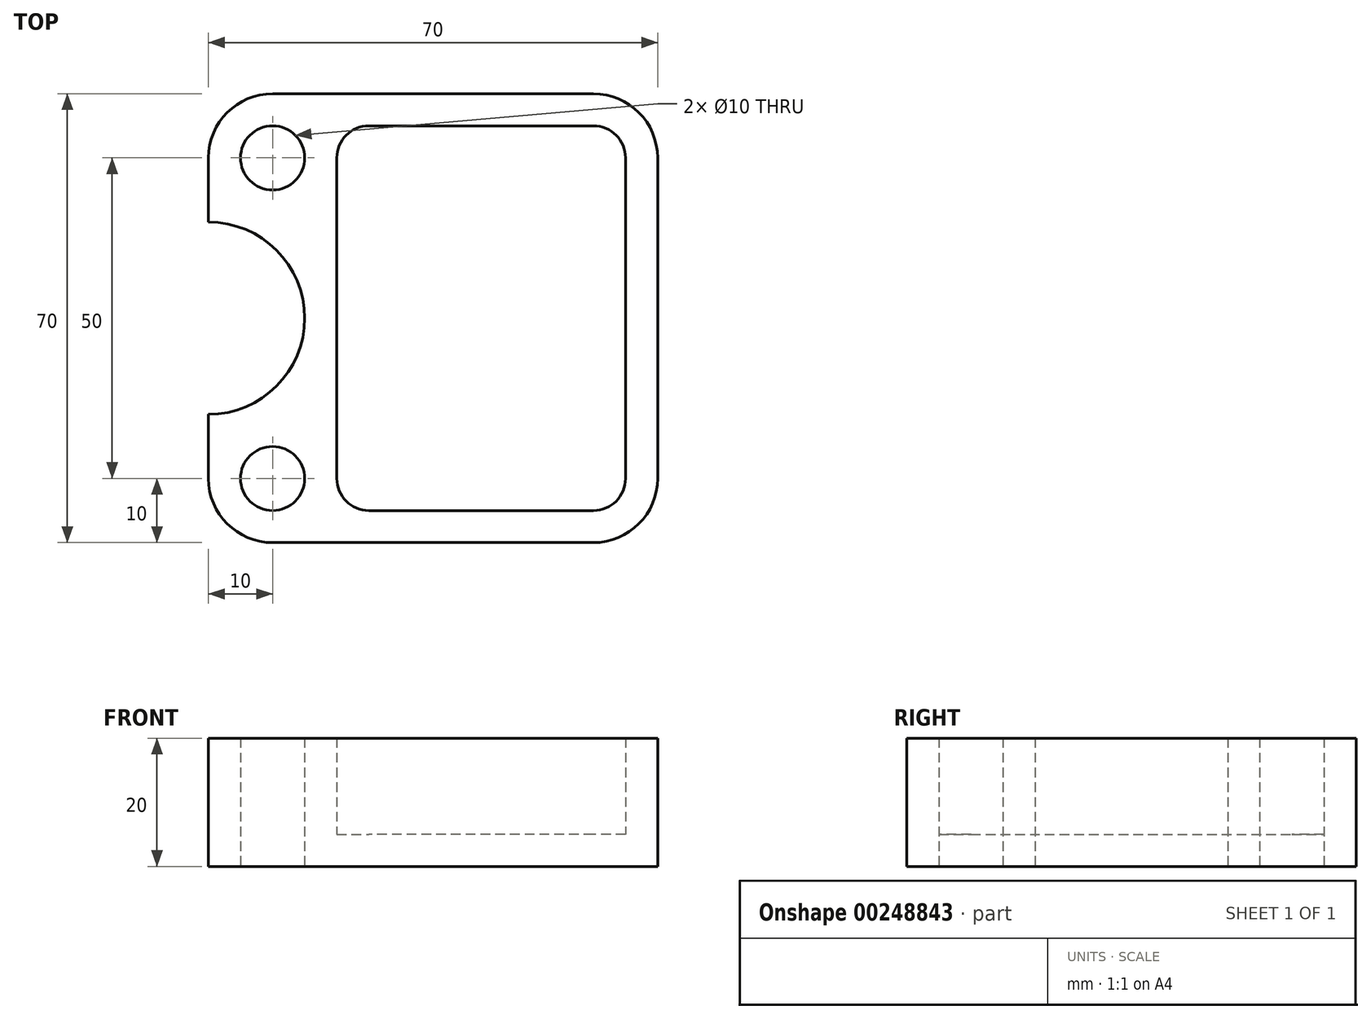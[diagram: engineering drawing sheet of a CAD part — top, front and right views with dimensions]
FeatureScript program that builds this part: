
annotation { "Feature Type Name" : "Feature", "Feature Type Description" : "" }
export const myFeature = defineFeature(function(context is Context, id is Id, definition is map)
    precondition{}
    {
        {
            var Q0;
            Q0=qCreatedBy(makeId("Top.planeOp"),FACE);
            var sketch = newSketch(context, id + "F0", { "sketchPlane" : qUnion([Q0])});
            skPoint(sketch, "E0.middle", {"position": v(0, 0) * mm});
            skCircle(sketch, "E1", {"center": v(-25, 25) * mm, "radius": 5 * mm});
            skCircle(sketch, "E2", {"center": v(-25, -25) * mm, "radius": 5 * mm});
            skArc(sketch, "E3", {"start": v(-35, -25) * mm, "mid": v(-32.07, -32.07) * mm, "end": v(-25, -35) * mm});
            skArc(sketch, "E4", {"start": v(-25, 35) * mm, "mid": v(-32.07, 32.07) * mm, "end": v(-35, 25) * mm});
            skLineSegment(sketch, "E5", {"start": v(-15, 25) * mm, "end": v(-15, -25) * mm});
            skArc(sketch, "E6", {"start": v(-15, 25) * mm, "mid": v(-13.54, 28.53) * mm, "end": v(-10, 30) * mm});
            skArc(sketch, "E7", {"start": v(25, -30) * mm, "mid": v(28.54, -28.54) * mm, "end": v(30, -25) * mm});
            skArc(sketch, "E8", {"start": v(30, 25) * mm, "mid": v(28.54, 28.54) * mm, "end": v(25, 30) * mm});
            skArc(sketch, "E9", {"start": v(35, 25) * mm, "mid": v(32.07, 32.07) * mm, "end": v(25, 35) * mm});
            skArc(sketch, "E10", {"start": v(35, -25) * mm, "mid": v(32.07, -32.07) * mm, "end": v(25, -35) * mm});
            skLineSegment(sketch, "E11", {"start": v(25, 35) * mm, "end": v(-25, 35) * mm});
            skLineSegment(sketch, "E12", {"start": v(-25, -35) * mm, "end": v(25, -35) * mm});
            skLineSegment(sketch, "E13", {"start": v(30, -25) * mm, "end": v(30, 25) * mm});
            skLineSegment(sketch, "E14", {"start": v(25, 30) * mm, "end": v(-10, 30) * mm});
            skArc(sketch, "E15", {"start": v(-15, -25) * mm, "mid": v(-13.54, -28.53) * mm, "end": v(-10, -30) * mm});
            skLineSegment(sketch, "E16", {"start": v(-10, -30) * mm, "end": v(25, -30) * mm});
            skLineSegment(sketch, "E17", {"start": v(35, 25) * mm, "end": v(35, -25) * mm});
            skArc(sketch, "E18", {"start": v(-35, 15) * mm, "mid": v(-20, 0) * mm, "end": v(-35, -15) * mm});
            skLineSegment(sketch, "E19", {"start": v(-35, 25) * mm, "end": v(-35, 15) * mm});
            skLineSegment(sketch, "E20", {"start": v(-35, -25) * mm, "end": v(-35, -15) * mm});
            skSolve(sketch);
        }
        {
            var Q0;
            Q0=makeQuery(id+"F0.imprint","IMPRINT",FACE,{"disambiguationData":[TD([[makeQuery(id+"F0.imprint","IMPRINT",EDGE,{"derivedFrom":sQuery(id+"F0.wireOp",EDGE,"E1")}),-1.0]])]});
            extrude(context, id + "F1", {"entities" : qUnion([Q0]), "depth" : 20 * mm});
        }
        {
            var Q0;
            Q0=makeQuery(id+"F0.imprint","IMPRINT",FACE,{"disambiguationData":[TD([[makeQuery(id+"F0.imprint","IMPRINT",EDGE,{"derivedFrom":sQuery(id+"F0.wireOp",EDGE,"E5")}),1.0]])]});
            extrude(context, id + "F2", {"entities" : qUnion([Q0]), "operationType" : NewBodyOperationType.ADD, "depth" : 5 * mm});
        }
    });
